# Revit family: Skystar_SK_24-4tr-HTA600_RFA2019
name_source: partatom
category: Mechanical Equipment
units: mm (PartAtom-declared; Revit-internal decimal feet)

## family parameters
Always vertical = Yes
Cut with Voids When Loaded = Yes
OmniClass Number = 23.75.00.00
OmniClass Title = Climate Control (HVAC)
Part Type = Normal
Room Calculation Point = Yes
Round Connector Dimension = Use Diameter
Shared = Yes
Work Plane-Based = Yes

## types (6) — shared parameters
4Pipes = Yes
A = 572 mm
D_QC_IN = 15 mm  [stored 0.0492126 ft]
D_Q_C_OUT = 15 mm  [stored 0.0492126 ft]
Default Elevation = 1219 mm
Description = Kazetový fancoil
Electric Battery = No
Foro controsoffitto = 582 mm
Lookup Table Name = SABIANA-SkyStar
Manufacturer = Hydronix
Qpa = 0 m³/h
S = 348 mm
THIN_def = 70 °C
Type Comments = Výměník čtyřtrubkový; motor asynchronní 3-otáčkový; čelní deska, mřížka, výdechy z ABS bílá RAL 9003
Type Image = 600x600.jpg
URL = www.hydronix.cz
cpa = 1.0050 J/(g·°C)
cph = 4.1860 J/(g·°C)
rho_a = 1.2000 kg/m³
rho_h = 1000.2970 kg/m³
side machine = 572 mm
zero-valued in all types: BVc

## per-type parameters (varying)
| type | Assembly Code | Model | Taglia |
| SK04 | SK04 (o.č.: 0079110)+HTA600 (o.č.: 9079020) | SK04 | 4 |
| SK14 | SK14 (o.č.: 0079010)+HTA600 (o.č.: 9079020) | SK 14 | 14 |
| SK34 | SK34 (o.č.: 0079012)+HTA600 (o.č.: 9079020) | SK34 | 34 |
| SK24 | SK24 (o.č.: 0079011)+HTA600 (o.č.: 9079020) | SK24 | 24 |
| SK26 | SK26 (o.č.: 0079016)+HTA600 (o.č.: 9079020) | SK26 | 26 |
| SK36 | SK36 (o.č.: 0079017)+HTA600 (o.č.: 9079020) | SK36 | 36 |

note: [stored X ft] marks values corroborated as IEEE doubles in the binary element streams (Revit-internal decimal feet)

## geometry (parser evidence)
native form markers: Blend x2
no freeform markers — native parametric forms only
